# Revit family: Harlequin Executive
name_source: partatom
category: Furniture
units: mm (PartAtom-declared; Revit-internal decimal feet)

## family parameters
Always vertical = Yes
Cut with Voids When Loaded = No
OmniClass Number = 23.40.20.00
OmniClass Title = General Furniture and Specialties
Room Calculation Point = No
Shared = Yes
Work Plane-Based = No

## types (3) — shared parameters
AccessibilityPerformance = Height Adjustable
Assembly Code = E2020200
AssetType = Moveable
Category = Pr_40_50_12_57: Office chairs
Color = Black
Constituents = Upholstered Seat and back, Seat mechanism, Castors
DurationUnit = Years
ExpectedLife = 10
Features = Optional Headrest, Height Adjustable Seat with Task Base. Fixed Steel Arms
Finish = Upholstered Seat and Back. Polished Aluminium Base
HighestSeatingHeight = 590 mm  [stored 1.9357 ft]
IfcExportAs = IfcFurnitureTypeEnum
IfcExportType = CHAIR
IsBuiltIn = No
Keynote = Pr_40_50_12_57
LowestSeatingHeight = 455 mm
MainColor = Defined by material specified
Manufacturer = Gresham
ManufacturerName = Gresham Office Furniture
ManufacturerURL = https://gof.co.uk
Material = Upholstered CHRM Foam Seat, Polished Aluminium Base
NBSDescription = Office chairs
NBSReference = 45-35-20/330
Name = OfficeChairs_Harlequin_Executive_Gresham
ProductInformation = https://gof.co.uk
ReplacementCost = 0
Shape = Square
Style = Task Chair
URL = https://gof.co.uk
Uniclass2015Code = Pr_40_50_12_57
Uniclass2015Title = Office chairs
Uniclass2015Version = Pr-Products v1.10
WarrantyDurationLabor = 5
WarrantyDurationParts = 5
WarrantyDurationUnit = Years
zero-valued in all types: Cost, SeatingHeight

## per-type parameters (varying)
| type | ArmType | BackType | Description | Model | ModelNumber | ModelReference | NominalHeight | NominalLength | NominalWidth | Size | TaskBase | Type Comments |
| Medium Back with Task Base | Nested_Gresham_OffcChrs_Harlequin_Executive_Arms : Arms | Nested_Gresham_OffcChrs_Harlequin_Executive_Back : LowBack | Medium Back with Task Base | HQME-SB1 | HQME-SB1 | Medium Back with Task Base | 980 mm  [stored 3.21522 ft] | 650 mm  [stored 2.13255 ft] | 650 mm  [stored 2.13255 ft] | (H) 950-1080mm x (L) 650mm x (W) 650mm | Yes | Medium Back with Task Base |
| Medium Back with Cantilever Base | Nested_Gresham_OffcChrs_Harlequin_Executive_Arms : Cantilever | Nested_Gresham_OffcChrs_Harlequin_Executive_Back : LowBack | Medium Back with CantilevercBase | HQEC-SB1 | HQEC-SB1 | Medium Back with CantilevercBase | 920 mm  [stored 3.01837 ft] | 640 mm  [stored 2.09974 ft] | 630 mm  [stored 2.06693 ft] | (H) 920mm x (L) 640mm x (W) 630mm | No | Medium Back with CantilevercBase |
| High Back with Task Base | Nested_Gresham_OffcChrs_Harlequin_Executive_Arms : Arms | Nested_Gresham_OffcChrs_Harlequin_Executive_Back : HighBack | High Back with Task Base | HQHE-SB1 | HQHE-SB1 | High Back with Task Base | 1400 mm  [stored 4.59318 ft] | 650 mm  [stored 2.13255 ft] | 650 mm  [stored 2.13255 ft] | (H) 1165-1300mm x (L) 650mm x (W) 650mm | Yes | High Back with Task Base |

note: [stored X ft] marks values corroborated as IEEE doubles in the binary element streams (Revit-internal decimal feet)

## geometry (parser evidence)
native form markers: Sweep x9
no freeform markers — native parametric forms only
